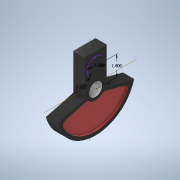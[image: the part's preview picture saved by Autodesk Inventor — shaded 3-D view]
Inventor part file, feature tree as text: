
AUTODESK INVENTOR PART (.ipt)
format: ipt  version: 2021.1 (Build 251245000, 245)  size: 192,000 bytes
history: native  units: in
note: dims shown in document units (in); Inventor stores cm internally (conversion verified against a paired STEP export)
features: extrude x6, sketch x4, projected_geometry x2, mirror x1
ambient origin geometry x8: Origin, YZ Plane, XZ Plane, XY Plane, X Axis, Y Axis, Z Axis, Center Point
bodies: Solid1 (feature_tree)
feature tree (13):
  extrude  "Extrusion1"  Depth=1.2in
  sketch  "Sketch2"  dims[d8=1.6in d9=0.0in d10=0.0in]
  extrude  "Extrusion2"  TaperAngle=0.0deg  [1 undecoded]
  extrude  "Extrusion3"  Depth=1.2in
  sketch  "Sketch3"  dims[d11=0.1in d12=0.0in d13=1.2in]
  extrude  "Extrusion4"  Depth=0.2in
  extrude  "Extrusion5"  TaperAngle=0.0deg  [1 undecoded]
  extrude  "Extrusion6"  Depth=0.1in TaperAngle=0.0deg
  mirror  "Mirror1"
  sketch  "Sketch1"  dims[d5=1.0in d6=0.0in d7=1.2in]
  sketch  "Sketch4"  dims[d14=1.6in d15=1.8in d16=0.0in d17=0.0in d18=0.1in d19=0.0in d20=6.6in d21=0.3in d22=0.3in d23=0.4in d24=1.7in d25=0.4in d26=0.2in d27=0.0in]
  projected_geometry  "Projected Loop1"
  projected_geometry  "Project Cut Edges1"
note: 2 required parameter values undecoded (feature->parameter linkage not recoverable at this tier; creation-order binding heuristic only, values carry confidence <= 0.55)
